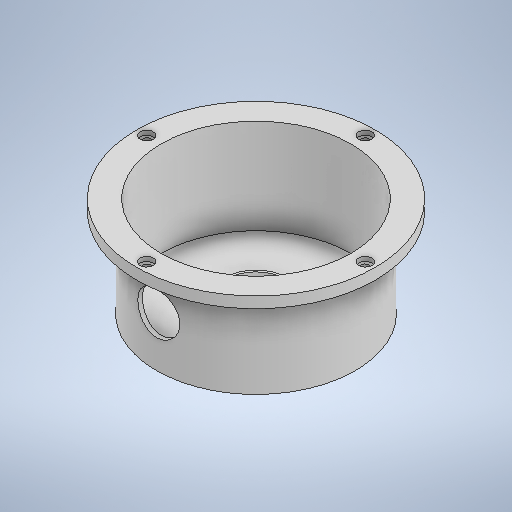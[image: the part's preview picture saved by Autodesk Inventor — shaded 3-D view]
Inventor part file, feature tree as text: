
AUTODESK INVENTOR PART (.ipt)
format: ipt  version: 2025.1 (Build 291241000, 241)  size: 349,184 bytes
history: native  units: mm
features: extrude x10, sketch x10, other x2
ambient origin geometry x8: Origin, YZ Plane, XZ Plane, XY Plane, X Axis, Y Axis, Z Axis, Center Point
bodies: Body1 (feature_tree)
feature tree (22):
  other  "Sólido1"
  extrude  "Extrusión1"  Depth=9.0mm
  extrude  "Extrusión2"  Depth=38.0mm TaperAngle=0.0deg
  extrude  "Extrusión3"  Depth=2.0mm
  extrude  "Extrusión4"  Depth=2.0mm
  extrude  "Extrusión5"  Depth=3.25mm
  extrude  "Extrusión6"  Depth=3.25mm
  extrude  "Extrusión7"  Depth=10.0mm TaperAngle=0.0deg
  other  "Empalme de cara1"
  extrude  "Extrusión8"  Depth=6.0mm
  extrude  "Extrusión9"  Depth=6.0mm
  extrude  "Extrusión10"  Depth=10.0mm
  sketch  "Boceto1"  dims[d0=90.0mm d1=9.0mm]
  sketch  "Boceto2"  dims[d2=5.0mm d3=0.0mm d5=38.0mm d6=0.0mm]
  sketch  "Boceto3"  dims[d7=2.0mm d8=2.0mm]
  sketch  "Boceto4"  dims[d9=2.0mm d10=0.0mm d11=4.5mm]
  sketch  "Boceto5"  dims[d12=90.0mm d13=3.25mm]
  sketch  "Boceto6"  dims[d14=3.25mm d15=3.25mm]
  sketch  "Boceto7"  dims[d16=3.25mm d17=10.0mm d18=0.0mm]
  sketch  "Boceto8"  dims[d19=6.0mm d20=6.0mm]
  sketch  "Boceto10"  dims[d21=6.0mm d22=6.0mm]
  sketch  "Boceto11"  dims[d23=2.0mm d24=0.0mm d33=26.25mm d34=5.0mm d35=0.0mm d36=1.0mm d37=26.25mm d38=5.0mm d39=0.0mm d40=5.0mm d41=10.0mm d42=0.0mm d43=200.0mm d44=10.0mm d45=19.1mm d46=70.0mm d47=0.0mm d48=10.0mm d49=0.0mm]
